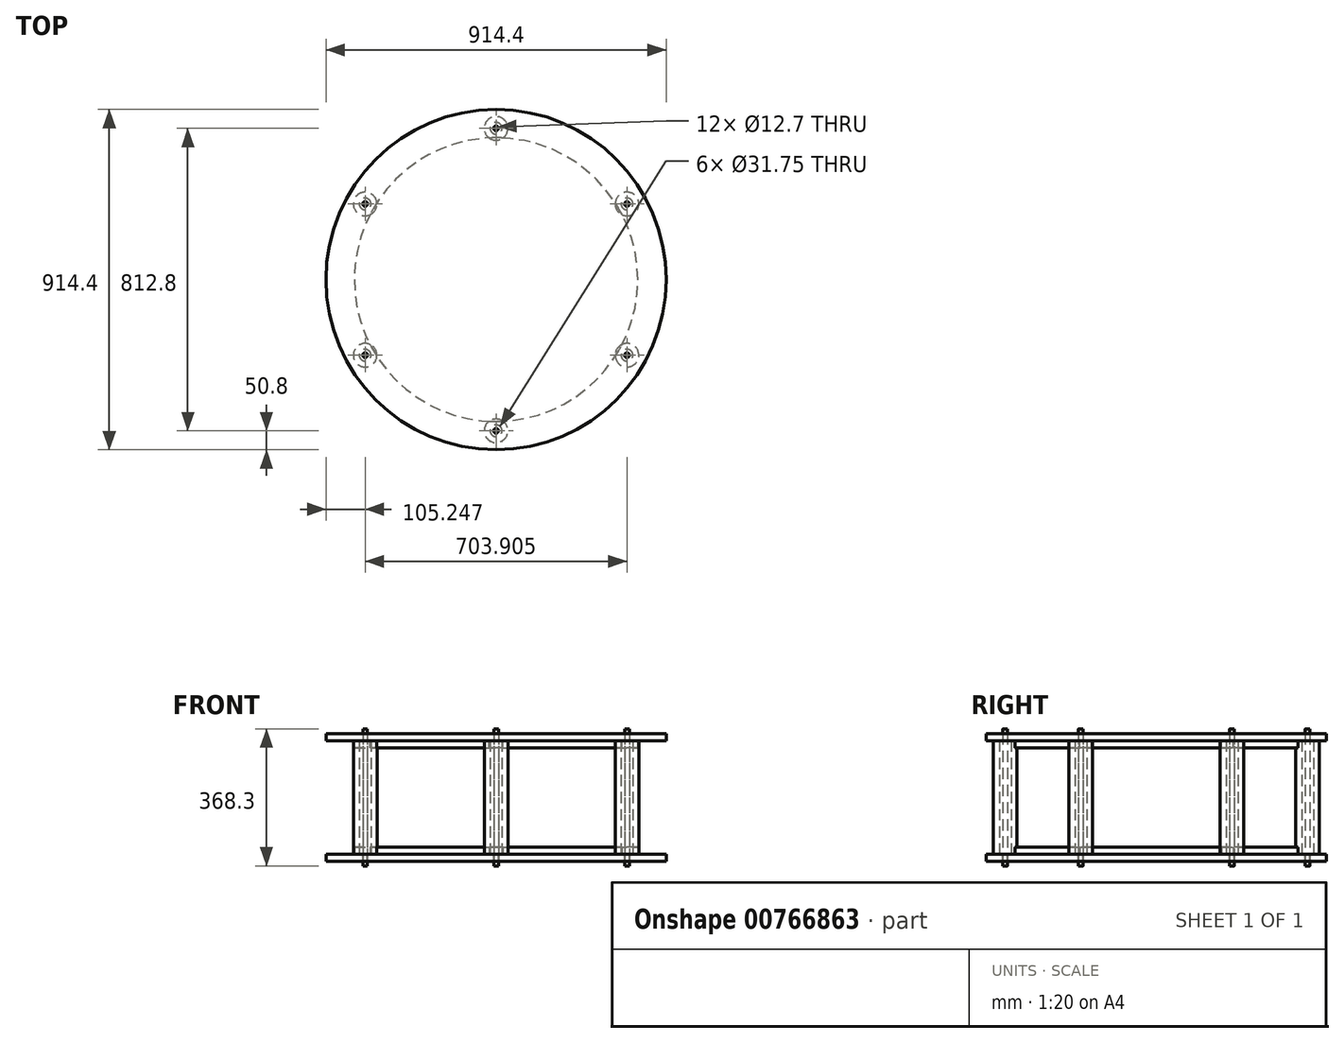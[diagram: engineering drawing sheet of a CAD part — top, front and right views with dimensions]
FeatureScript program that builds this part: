
annotation { "Feature Type Name" : "Feature", "Feature Type Description" : "" }
export const myFeature = defineFeature(function(context is Context, id is Id, definition is map)
    precondition{}
    {
        {
            assignVariable(context, id + "F0", {"name" : "drumDepth", "anyValue" : 304.8 * mm});
        }
        {
            assignVariable(context, id + "F1", {"name" : "plywoodThickness", "anyValue" : 19.05 * mm});
        }
        {
            var Q0;
            Q0=qCreatedBy(makeId("Top.planeOp"),FACE);
            var sketch = newSketch(context, id + "F2", { "sketchPlane" : qUnion([Q0])});
            skCircle(sketch, "E0", {"center": v(0, 0) * mm, "radius": 457.2 * mm});
            skCircle(sketch, "E1", {"center": v(0, 0) * mm, "radius": 381 * mm, "construction": true});
            skLineSegment(sketch, "E2", {"start": v(0, 381) * mm, "end": v(0, 457.2) * mm, "construction": true});
            skCircle(sketch, "E3", {"center": v(0, 406.4) * mm, "radius": 6.35 * mm});
            skCircle(sketch, "E4", {"center": v(0, 406.4) * mm, "radius": 31.75 * mm});
            skCircle(sketch, "E5", {"center": v(0, 406.4) * mm, "radius": 15.88 * mm});
            skCircle(sketch, "E6.1.0", {"center": v(-351.95, 203.2) * mm, "radius": 31.75 * mm});
            skCircle(sketch, "E6.1.1", {"center": v(-351.95, 203.2) * mm, "radius": 15.88 * mm});
            skCircle(sketch, "E6.1.2", {"center": v(-351.95, 203.2) * mm, "radius": 6.35 * mm});
            skCircle(sketch, "E6.2.0", {"center": v(-351.95, -203.2) * mm, "radius": 31.75 * mm});
            skCircle(sketch, "E6.2.1", {"center": v(-351.95, -203.2) * mm, "radius": 15.88 * mm});
            skCircle(sketch, "E6.2.2", {"center": v(-351.95, -203.2) * mm, "radius": 6.35 * mm});
            skCircle(sketch, "E6.3.0", {"center": v(0, -406.4) * mm, "radius": 31.75 * mm});
            skCircle(sketch, "E6.3.1", {"center": v(0, -406.4) * mm, "radius": 15.88 * mm});
            skCircle(sketch, "E6.3.2", {"center": v(0, -406.4) * mm, "radius": 6.35 * mm});
            skCircle(sketch, "E6.4.0", {"center": v(351.95, -203.2) * mm, "radius": 31.75 * mm});
            skCircle(sketch, "E6.4.1", {"center": v(351.95, -203.2) * mm, "radius": 15.88 * mm});
            skCircle(sketch, "E6.4.2", {"center": v(351.95, -203.2) * mm, "radius": 6.35 * mm});
            skCircle(sketch, "E6.5.0", {"center": v(351.95, 203.2) * mm, "radius": 31.75 * mm});
            skCircle(sketch, "E6.5.1", {"center": v(351.95, 203.2) * mm, "radius": 15.88 * mm});
            skCircle(sketch, "E6.5.2", {"center": v(351.95, 203.2) * mm, "radius": 6.35 * mm});
            skSolve(sketch);
        }
        {
            var Q0;
            Q0=makeQuery(id+"F2.imprint","IMPRINT",FACE,{"disambiguationData":[TD([[makeQuery(id+"F2.imprint","IMPRINT",EDGE,{"derivedFrom":sQuery(id+"F2.wireOp",EDGE,"E0")}),1.0]])]});
            var Q1;
            Q1=makeQuery(id+"F2.imprint","IMPRINT",FACE,{"disambiguationData":[TD([[makeQuery(id+"F2.imprint","IMPRINT",EDGE,{"derivedFrom":sQuery(id+"F2.wireOp",EDGE,"E6.5.0")}),1.0]])]});
            var Q2;
            Q2=makeQuery(id+"F2.imprint","IMPRINT",FACE,{"disambiguationData":[TD([[makeQuery(id+"F2.imprint","IMPRINT",EDGE,{"derivedFrom":sQuery(id+"F2.wireOp",EDGE,"E6.5.1")}),1.0]])]});
            var Q3;
            Q3=makeQuery(id+"F2.imprint","IMPRINT",FACE,{"disambiguationData":[TD([[makeQuery(id+"F2.imprint","IMPRINT",EDGE,{"derivedFrom":sQuery(id+"F2.wireOp",EDGE,"E6.4.0")}),1.0]])]});
            var Q4;
            Q4=makeQuery(id+"F2.imprint","IMPRINT",FACE,{"disambiguationData":[TD([[makeQuery(id+"F2.imprint","IMPRINT",EDGE,{"derivedFrom":sQuery(id+"F2.wireOp",EDGE,"E6.4.1")}),1.0]])]});
            var Q5;
            Q5=makeQuery(id+"F2.imprint","IMPRINT",FACE,{"disambiguationData":[TD([[makeQuery(id+"F2.imprint","IMPRINT",EDGE,{"derivedFrom":sQuery(id+"F2.wireOp",EDGE,"E4")}),1.0]])]});
            var Q6;
            Q6=makeQuery(id+"F2.imprint","IMPRINT",FACE,{"disambiguationData":[TD([[makeQuery(id+"F2.imprint","IMPRINT",EDGE,{"derivedFrom":sQuery(id+"F2.wireOp",EDGE,"E3")}),-1.0]])]});
            var Q7;
            Q7=makeQuery(id+"F2.imprint","IMPRINT",FACE,{"disambiguationData":[TD([[makeQuery(id+"F2.imprint","IMPRINT",EDGE,{"derivedFrom":sQuery(id+"F2.wireOp",EDGE,"E6.1.0")}),1.0]])]});
            var Q8;
            Q8=makeQuery(id+"F2.imprint","IMPRINT",FACE,{"disambiguationData":[TD([[makeQuery(id+"F2.imprint","IMPRINT",EDGE,{"derivedFrom":sQuery(id+"F2.wireOp",EDGE,"E6.1.1")}),1.0]])]});
            var Q9;
            Q9=makeQuery(id+"F2.imprint","IMPRINT",FACE,{"disambiguationData":[TD([[makeQuery(id+"F2.imprint","IMPRINT",EDGE,{"derivedFrom":sQuery(id+"F2.wireOp",EDGE,"E6.2.0")}),1.0]])]});
            var Q10;
            Q10=makeQuery(id+"F2.imprint","IMPRINT",FACE,{"disambiguationData":[TD([[makeQuery(id+"F2.imprint","IMPRINT",EDGE,{"derivedFrom":sQuery(id+"F2.wireOp",EDGE,"E6.2.1")}),1.0]])]});
            var Q11;
            Q11=makeQuery(id+"F2.imprint","IMPRINT",FACE,{"disambiguationData":[TD([[makeQuery(id+"F2.imprint","IMPRINT",EDGE,{"derivedFrom":sQuery(id+"F2.wireOp",EDGE,"E6.3.0")}),1.0]])]});
            var Q12;
            Q12=makeQuery(id+"F2.imprint","IMPRINT",FACE,{"disambiguationData":[TD([[makeQuery(id+"F2.imprint","IMPRINT",EDGE,{"derivedFrom":sQuery(id+"F2.wireOp",EDGE,"E6.3.1")}),1.0]])]});
            extrude(context, id + "F3", {"entities" : qUnion([Q0, Q1, Q2, Q3, Q4, Q5, Q6, Q7, Q8, Q9, Q10, Q11, Q12]), "oppositeDirection" : true, "depth" : 19.05 * mm, "offsetDistance" : 25.4 * mm});
        }
        {
            var Q0;
            Q0=makeQuery(id+"F2.imprint","IMPRINT",FACE,{"disambiguationData":[TD([[makeQuery(id+"F2.imprint","IMPRINT",EDGE,{"derivedFrom":sQuery(id+"F2.wireOp",EDGE,"E6.4.0")}),1.0]])]});
            var Q1;
            Q1=makeQuery(id+"F2.imprint","IMPRINT",FACE,{"disambiguationData":[TD([[makeQuery(id+"F2.imprint","IMPRINT",EDGE,{"derivedFrom":sQuery(id+"F2.wireOp",EDGE,"E6.3.0")}),1.0]])]});
            var Q2;
            Q2=makeQuery(id+"F2.imprint","IMPRINT",FACE,{"disambiguationData":[TD([[makeQuery(id+"F2.imprint","IMPRINT",EDGE,{"derivedFrom":sQuery(id+"F2.wireOp",EDGE,"E6.2.0")}),1.0]])]});
            var Q3;
            Q3=makeQuery(id+"F2.imprint","IMPRINT",FACE,{"disambiguationData":[TD([[makeQuery(id+"F2.imprint","IMPRINT",EDGE,{"derivedFrom":sQuery(id+"F2.wireOp",EDGE,"E6.1.0")}),1.0]])]});
            var Q4;
            Q4=makeQuery(id+"F2.imprint","IMPRINT",FACE,{"disambiguationData":[TD([[makeQuery(id+"F2.imprint","IMPRINT",EDGE,{"derivedFrom":sQuery(id+"F2.wireOp",EDGE,"E4")}),1.0]])]});
            var Q5;
            Q5=makeQuery(id+"F2.imprint","IMPRINT",FACE,{"disambiguationData":[TD([[makeQuery(id+"F2.imprint","IMPRINT",EDGE,{"derivedFrom":sQuery(id+"F2.wireOp",EDGE,"E6.5.0")}),1.0]])]});
            extrude(context, id + "F4", {"entities" : qUnion([Q0, Q1, Q2, Q3, Q4, Q5]), "depth" : getVariable(context, 'drumDepth'), "offsetDistance" : 25.4 * mm});
        }
        {
            var Q0;
            Q0=makeQuery(id+"F3.opExtrude","CAP_FACE",FACE,{"disambiguationData":[OSD([sQuery(id+"F2.wireOp",EDGE,"E0"),sQuery(id+"F2.wireOp",EDGE,"E3"),sQuery(id+"F2.wireOp",EDGE,"E6.1.2"),sQuery(id+"F2.wireOp",EDGE,"E6.2.2"),sQuery(id+"F2.wireOp",EDGE,"E6.3.2"),sQuery(id+"F2.wireOp",EDGE,"E6.4.2"),sQuery(id+"F2.wireOp",EDGE,"E6.5.2")])],"isStart":true});
            var sketch = newSketch(context, id + "F5", { "sketchPlane" : qUnion([Q0])});
            skCircle(sketch, "E7", {"center": v(0, 0) * mm, "radius": 381 * mm});
            skSolve(sketch);
        }
        {
            var Q0;
            Q0=makeQuery(id+"F5.imprint","IMPRINT",FACE,{"disambiguationData":[TD([[makeQuery(id+"F5.imprint","IMPRINT",EDGE,{"derivedFrom":sQuery(id+"F5.wireOp",EDGE,"E7")}),1.0]])]});
            extrude(context, id + "F6", {"entities" : qUnion([Q0]), "depth" : 19.05 * mm, "offsetDistance" : 25.4 * mm});
        }
        {
            var Q0;
            Q0=qCreatedBy(makeId("Top.planeOp"),FACE);
            cPlane(context, id + "F7", {"entities" : qUnion([Q0]), "cplaneType" : CPlaneType.OFFSET, "offset" : getVariable(context, 'drumDepth') / 2, "width" : 152.4 * mm, "height" : 152.4 * mm});
        }
        {
            var Q0;
            Q0=makeQuery(id+"F3.opExtrude","SWEPT_BODY",BODY,{"disambiguationData":[OSD([sQuery(id+"F2.wireOp",EDGE,"E0"),sQuery(id+"F2.wireOp",EDGE,"E3"),sQuery(id+"F2.wireOp",EDGE,"E6.1.2"),sQuery(id+"F2.wireOp",EDGE,"E6.2.2"),sQuery(id+"F2.wireOp",EDGE,"E6.3.2"),sQuery(id+"F2.wireOp",EDGE,"E6.4.2"),sQuery(id+"F2.wireOp",EDGE,"E6.5.2")])]});
            var Q1;
            Q1=makeQuery(id+"F6.opExtrude","SWEPT_BODY",BODY,{"disambiguationData":[OSD([sQuery(id+"F5.wireOp",EDGE,"E7")])]});
            var Q2;
            Q2=qCreatedBy(id+"F7.planeOp",FACE);
            mirror(context, id + "F8", {"entities" : qUnion([Q0, Q1]), "mirrorPlane" : qUnion([Q2])});
        }
        {
            var Q0;
            Q0=makeQuery(id+"F6.opExtrude","SWEPT_BODY",BODY,{"disambiguationData":[OSD([sQuery(id+"F5.wireOp",EDGE,"E7")])]});
            var Q1;
            Q1=makeQuery(id+"F8.opPattern","COPY",BODY,{"derivedFrom":makeQuery(id+"F6.opExtrude","SWEPT_BODY",BODY,{"disambiguationData":[OSD([sQuery(id+"F5.wireOp",EDGE,"E7")])]}),"instanceName":"1"});
            var Q2;
            Q2=makeQuery(id+"F4.opExtrude","SWEPT_BODY",BODY,{"disambiguationData":[OSD([sQuery(id+"F2.wireOp",EDGE,"E6.2.0"),sQuery(id+"F2.wireOp",EDGE,"E6.2.1")])]});
            var Q3;
            Q3=makeQuery(id+"F4.opExtrude","SWEPT_BODY",BODY,{"disambiguationData":[OSD([sQuery(id+"F2.wireOp",EDGE,"E6.1.0"),sQuery(id+"F2.wireOp",EDGE,"E6.1.1")])]});
            var Q4;
            Q4=makeQuery(id+"F4.opExtrude","SWEPT_BODY",BODY,{"disambiguationData":[OSD([sQuery(id+"F2.wireOp",EDGE,"E4"),sQuery(id+"F2.wireOp",EDGE,"E5")])]});
            var Q5;
            Q5=makeQuery(id+"F4.opExtrude","SWEPT_BODY",BODY,{"disambiguationData":[OSD([sQuery(id+"F2.wireOp",EDGE,"E6.5.0"),sQuery(id+"F2.wireOp",EDGE,"E6.5.1")])]});
            var Q6;
            Q6=makeQuery(id+"F4.opExtrude","SWEPT_BODY",BODY,{"disambiguationData":[OSD([sQuery(id+"F2.wireOp",EDGE,"E6.4.0"),sQuery(id+"F2.wireOp",EDGE,"E6.4.1")])]});
            var Q7;
            Q7=makeQuery(id+"F4.opExtrude","SWEPT_BODY",BODY,{"disambiguationData":[OSD([sQuery(id+"F2.wireOp",EDGE,"E6.3.0"),sQuery(id+"F2.wireOp",EDGE,"E6.3.1")])]});
            booleanBodies(context, id + "F9", {"operationType" : BooleanOperationType.SUBTRACTION, "tools" : qUnion([Q0, Q1]), "targets" : qUnion([Q2, Q3, Q4, Q5, Q6, Q7]), "keepTools" : true});
        }
        {
            var Q0;
            Q0=makeQuery(id+"F2.imprint","IMPRINT",FACE,{"disambiguationData":[TD([[makeQuery(id+"F2.imprint","IMPRINT",EDGE,{"derivedFrom":sQuery(id+"F2.wireOp",EDGE,"E3")}),1.0]])]});
            var Q1;
            Q1=makeQuery(id+"F2.imprint","IMPRINT",FACE,{"disambiguationData":[TD([[makeQuery(id+"F2.imprint","IMPRINT",EDGE,{"derivedFrom":sQuery(id+"F2.wireOp",EDGE,"E6.1.2")}),1.0]])]});
            var Q2;
            Q2=makeQuery(id+"F2.imprint","IMPRINT",FACE,{"disambiguationData":[TD([[makeQuery(id+"F2.imprint","IMPRINT",EDGE,{"derivedFrom":sQuery(id+"F2.wireOp",EDGE,"E6.2.2")}),1.0]])]});
            var Q3;
            Q3=makeQuery(id+"F2.imprint","IMPRINT",FACE,{"disambiguationData":[TD([[makeQuery(id+"F2.imprint","IMPRINT",EDGE,{"derivedFrom":sQuery(id+"F2.wireOp",EDGE,"E6.3.2")}),1.0]])]});
            var Q4;
            Q4=makeQuery(id+"F2.imprint","IMPRINT",FACE,{"disambiguationData":[TD([[makeQuery(id+"F2.imprint","IMPRINT",EDGE,{"derivedFrom":sQuery(id+"F2.wireOp",EDGE,"E6.4.2")}),1.0]])]});
            var Q5;
            Q5=makeQuery(id+"F2.imprint","IMPRINT",FACE,{"disambiguationData":[TD([[makeQuery(id+"F2.imprint","IMPRINT",EDGE,{"derivedFrom":sQuery(id+"F2.wireOp",EDGE,"E6.5.2")}),1.0]])]});
            extrude(context, id + "F10", {"entities" : qUnion([Q0, Q1, Q2, Q3, Q4, Q5]), "depth" : getVariable(context, 'drumDepth') + getVariable(context, 'plywoodThickness') + 12.7 * mm, "offsetDistance" : 25.4 * mm, "hasSecondDirection" : true, "secondDirectionOppositeDirection" : true, "secondDirectionDepth" : getVariable(context, 'plywoodThickness') + 12.7 * mm});
        }
    });
